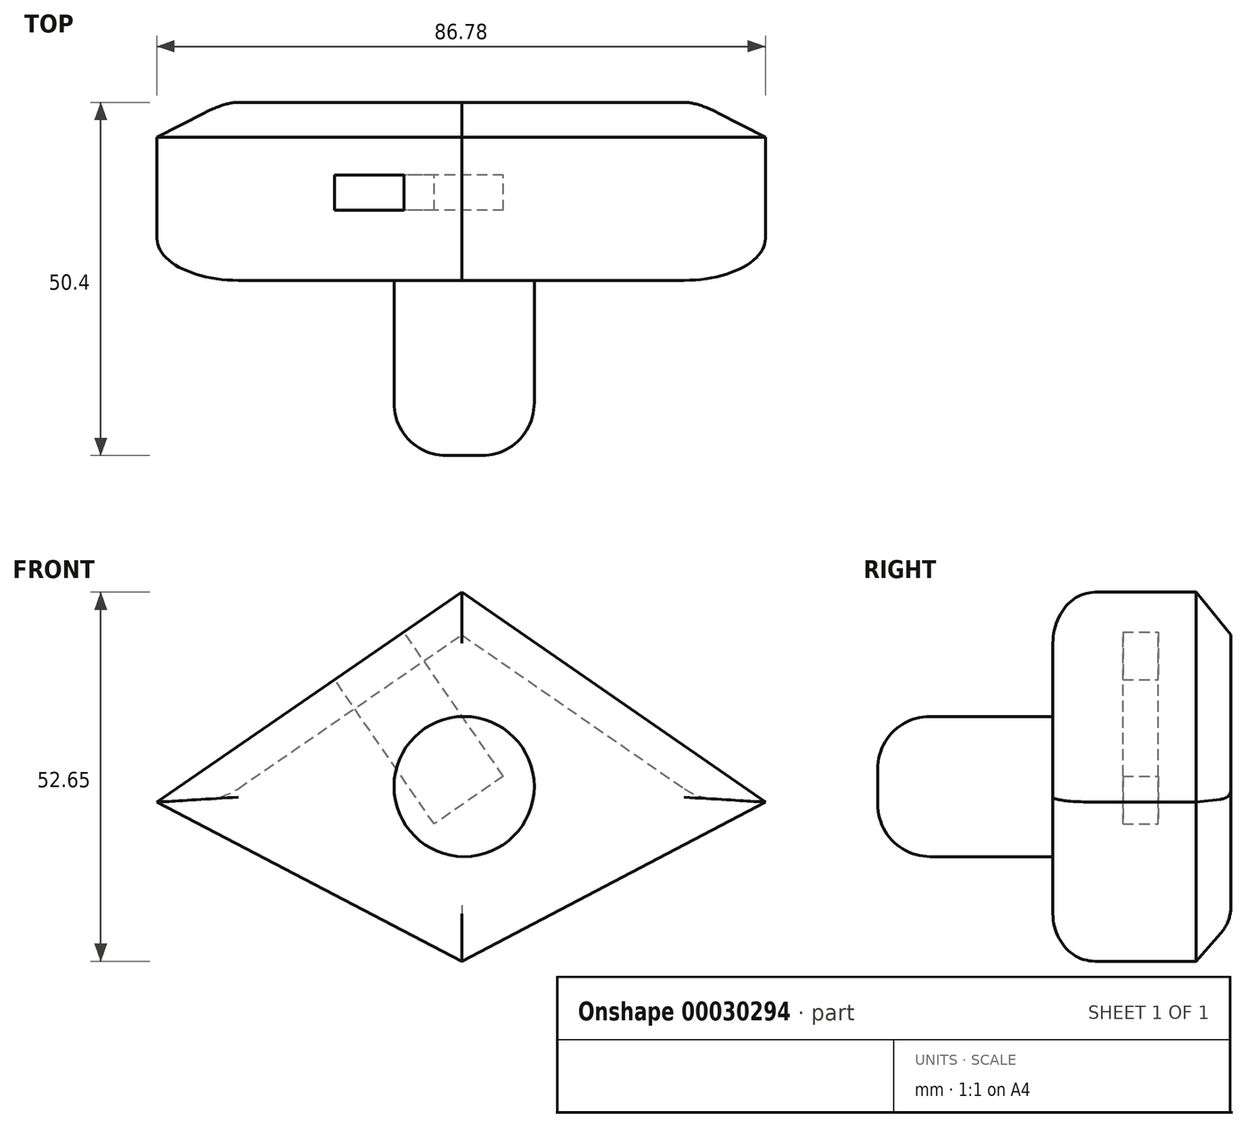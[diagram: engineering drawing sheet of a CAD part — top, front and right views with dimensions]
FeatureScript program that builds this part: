
annotation { "Feature Type Name" : "Feature", "Feature Type Description" : "" }
export const myFeature = defineFeature(function(context is Context, id is Id, definition is map)
    precondition{}
    {
        {
            var Q0;
            Q0=qCreatedBy(makeId("Front.planeOp"),FACE);
            var sketch = newSketch(context, id + "F0", { "sketchPlane" : qUnion([Q0])});
            skLineSegment(sketch, "E0", {"start": v(0, 29.95) * mm, "end": v(-43.47, 0) * mm});
            skLineSegment(sketch, "E1", {"start": v(-43.47, 0) * mm, "end": v(0, -22.7) * mm});
            skLineSegment(sketch, "E2", {"start": v(0, -22.7) * mm, "end": v(43.3, 0) * mm});
            skLineSegment(sketch, "E3", {"start": v(43.3, 0) * mm, "end": v(0, 29.95) * mm});
            skSolve(sketch);
        }
        {
            var Q0;
            Q0=makeQuery(id+"F0.imprint","IMPRINT",FACE,{"disambiguationData":[TD([[makeQuery(id+"F0.imprint","IMPRINT",EDGE,{"derivedFrom":sQuery(id+"F0.wireOp",EDGE,"E0")}),1.0]])]});
            extrude(context, id + "F1", {"entities" : qUnion([Q0]), "depth" : 25.4 * mm});
        }
        {
            var Q0;
            Q0=makeQuery(id+"F1.opExtrude","CAP_EDGE",EDGE,{"disambiguationData":[OSD([sQuery(id+"F0.wireOp",EDGE,"E0")])],"isStart":true});
            var Q1;
            Q1=makeQuery(id+"F1.opExtrude","CAP_EDGE",EDGE,{"disambiguationData":[OSD([sQuery(id+"F0.wireOp",EDGE,"E1")])],"isStart":true});
            var Q2;
            Q2=makeQuery(id+"F1.opExtrude","CAP_EDGE",EDGE,{"disambiguationData":[OSD([sQuery(id+"F0.wireOp",EDGE,"E2")])],"isStart":true});
            var Q3;
            Q3=makeQuery(id+"F1.opExtrude","CAP_EDGE",EDGE,{"disambiguationData":[OSD([sQuery(id+"F0.wireOp",EDGE,"E3")])],"isStart":true});
            chamfer(context, id + "F2", {"entities" : qUnion([Q0, Q1, Q2, Q3]), "width" : 5 * mm, "tangentPropagation" : true});
        }
        {
            var Q0;
            Q0=makeQuery(id+"F1.opExtrude","CAP_EDGE",EDGE,{"disambiguationData":[OSD([sQuery(id+"F0.wireOp",EDGE,"E0")])],"isStart":false});
            var Q1;
            Q1=makeQuery(id+"F1.opExtrude","CAP_EDGE",EDGE,{"disambiguationData":[OSD([sQuery(id+"F0.wireOp",EDGE,"E3")])],"isStart":false});
            var Q2;
            Q2=makeQuery(id+"F1.opExtrude","CAP_EDGE",EDGE,{"disambiguationData":[OSD([sQuery(id+"F0.wireOp",EDGE,"E2")])],"isStart":false});
            var Q3;
            Q3=makeQuery(id+"F1.opExtrude","CAP_EDGE",EDGE,{"disambiguationData":[OSD([sQuery(id+"F0.wireOp",EDGE,"E1")])],"isStart":false});
            fillet(context, id + "F3", {"entities" : qUnion([Q0, Q1, Q2, Q3]), "radius" : 6 * mm, "tangentPropagation" : true, "allowEdgeOverflow" : false});
        }
        {
            var Q0;
            Q0=makeQuery(id+"F1.opExtrude","SWEPT_FACE",FACE,{"disambiguationData":[OSD([sQuery(id+"F0.wireOp",EDGE,"E0")])]});
            var sketch = newSketch(context, id + "F4", { "sketchPlane" : qUnion([Q0])});
            skLineSegment(sketch, "E4.0", {"start": v(17, -19.4) * mm, "end": v(17, -5) * mm});
            skLineSegment(sketch, "E5.0", {"start": v(17, -5) * mm, "end": v(-35.8, -5) * mm});
            skLineSegment(sketch, "E6.0", {"start": v(-35.8, -19.4) * mm, "end": v(17, -19.4) * mm});
            skLineSegment(sketch, "E7.0", {"start": v(-35.8, -19.4) * mm, "end": v(-35.8, -5) * mm});
            skLineSegment(sketch, "E8.bottom", {"start": v(7, -15.4) * mm, "end": v(-5, -15.4) * mm});
            skLineSegment(sketch, "E8.top", {"start": v(7, -10.4) * mm, "end": v(-5, -10.4) * mm});
            skLineSegment(sketch, "E8.left", {"start": v(7, -15.4) * mm, "end": v(7, -10.4) * mm});
            skLineSegment(sketch, "E8.right", {"start": v(-5, -15.4) * mm, "end": v(-5, -10.4) * mm});
            skSolve(sketch);
        }
        {
            var Q0;
            Q0=makeQuery(id+"F4.imprint","IMPRINT",FACE,{"disambiguationData":[TD([[makeQuery(id+"F4.imprint","IMPRINT",EDGE,{"derivedFrom":sQuery(id+"F4.wireOp",EDGE,"E8.bottom")}),-1.0]])]});
            extrude(context, id + "F5", {"entities" : qUnion([Q0]), "operationType" : NewBodyOperationType.REMOVE, "oppositeDirection" : true, "depth" : 25 * mm});
        }
        {
            var Q0;
            {var subQ0=sQuery(id+"F0.wireOp",EDGE,"E1");Q0=makeQuery(id+"F2.opChamfer","BLEND_EDGE",EDGE,{"blendedFrom":[makeQuery(id+"F1.opExtrude","CAP_EDGE",EDGE,{"disambiguationData":[OSD([subQ0])],"isStart":true}),makeQuery(id+"F1.opExtrude","CAP_FACE",FACE,{"disambiguationData":[OSD([sQuery(id+"F0.wireOp",EDGE,"E0"),subQ0,sQuery(id+"F0.wireOp",EDGE,"E2"),sQuery(id+"F0.wireOp",EDGE,"E3")])],"isStart":true})],"blendedInto":[makeQuery(id+"F1.opExtrude","CAP_FACE",FACE,{"disambiguationData":[OSD([sQuery(id+"F0.wireOp",EDGE,"E0"),subQ0,sQuery(id+"F0.wireOp",EDGE,"E2"),sQuery(id+"F0.wireOp",EDGE,"E3")])],"isStart":true})]});}
            var Q1;
            {var subQ0=sQuery(id+"F0.wireOp",EDGE,"E2");Q1=makeQuery(id+"F2.opChamfer","BLEND_EDGE",EDGE,{"blendedFrom":[makeQuery(id+"F1.opExtrude","CAP_EDGE",EDGE,{"disambiguationData":[OSD([subQ0])],"isStart":true}),makeQuery(id+"F1.opExtrude","CAP_FACE",FACE,{"disambiguationData":[OSD([sQuery(id+"F0.wireOp",EDGE,"E0"),sQuery(id+"F0.wireOp",EDGE,"E1"),subQ0,sQuery(id+"F0.wireOp",EDGE,"E3")])],"isStart":true})],"blendedInto":[makeQuery(id+"F1.opExtrude","CAP_FACE",FACE,{"disambiguationData":[OSD([sQuery(id+"F0.wireOp",EDGE,"E0"),sQuery(id+"F0.wireOp",EDGE,"E1"),subQ0,sQuery(id+"F0.wireOp",EDGE,"E3")])],"isStart":true})]});}
            fillet(context, id + "F6", {"entities" : qUnion([Q0, Q1]), "radius" : 5 * mm, "tangentPropagation" : true, "allowEdgeOverflow" : false});
        }
        {
            var Q0;
            Q0=makeQuery(id+"F1.opExtrude","CAP_FACE",FACE,{"disambiguationData":[OSD([sQuery(id+"F0.wireOp",EDGE,"E0"),sQuery(id+"F0.wireOp",EDGE,"E1"),sQuery(id+"F0.wireOp",EDGE,"E2"),sQuery(id+"F0.wireOp",EDGE,"E3")])],"isStart":false});
            var sketch = newSketch(context, id + "F7", { "sketchPlane" : qUnion([Q0])});
            skCircle(sketch, "E9", {"center": v(0.34, 2.23) * mm, "radius": 10 * mm});
            skSolve(sketch);
        }
        {
            var Q0;
            Q0=makeQuery(id+"F7.imprint","IMPRINT",FACE,{"disambiguationData":[TD([[makeQuery(id+"F7.imprint","IMPRINT",EDGE,{"derivedFrom":sQuery(id+"F7.wireOp",EDGE,"E9")}),1.0]])]});
            extrude(context, id + "F8", {"entities" : qUnion([Q0]), "operationType" : NewBodyOperationType.ADD, "depth" : 25 * mm});
        }
        {
            var Q0;
            Q0=makeQuery(id+"F8.opExtrude","CAP_EDGE",EDGE,{"disambiguationData":[OSD([sQuery(id+"F7.wireOp",EDGE,"E9")])],"isStart":false});
            fillet(context, id + "F9", {"entities" : qUnion([Q0]), "radius" : 7.5 * mm, "tangentPropagation" : true, "allowEdgeOverflow" : false});
        }
    });
